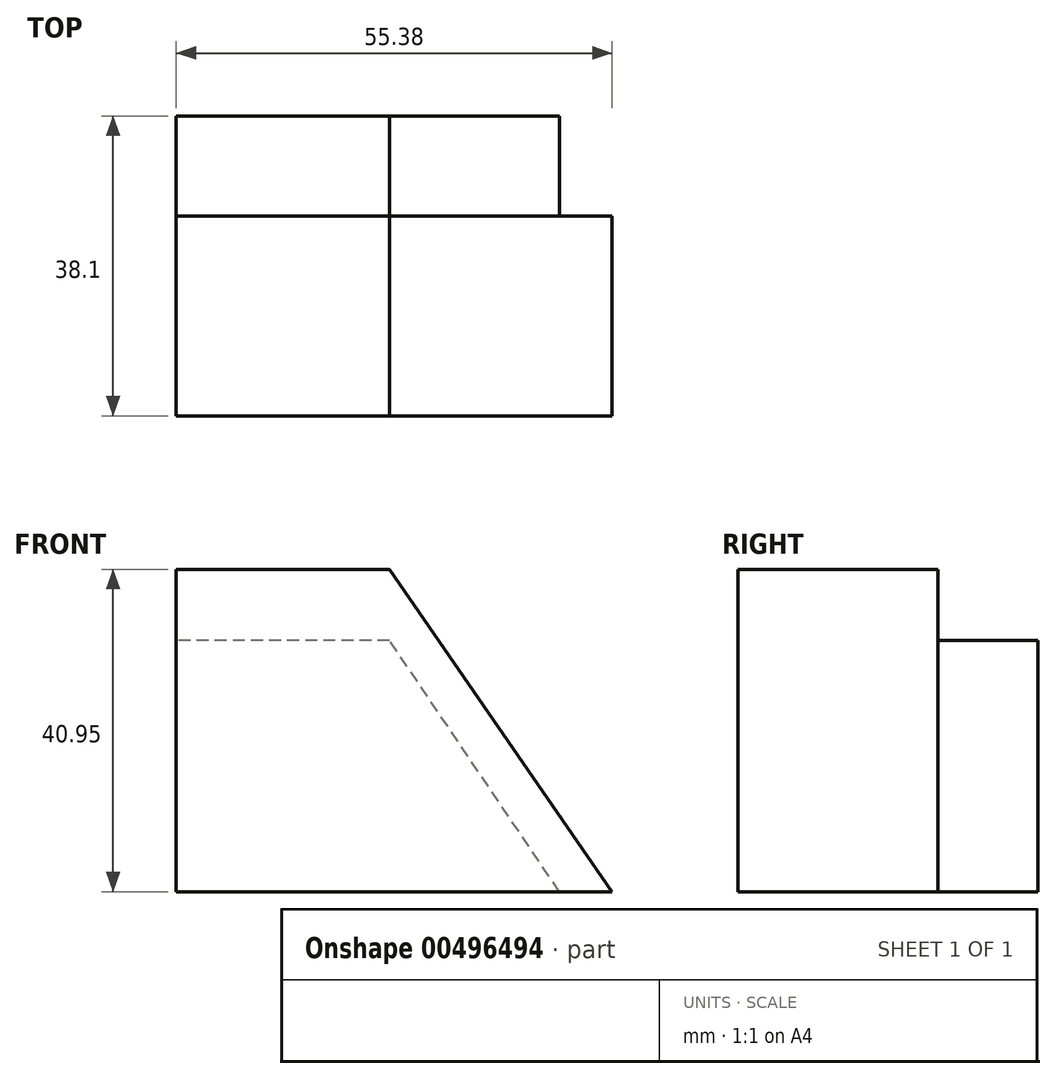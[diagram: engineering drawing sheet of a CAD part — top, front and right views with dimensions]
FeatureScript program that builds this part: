
annotation { "Feature Type Name" : "Feature", "Feature Type Description" : "" }
export const myFeature = defineFeature(function(context is Context, id is Id, definition is map)
    precondition{}
    {
        {
            var Q0;
            Q0=qCreatedBy(makeId("Front.planeOp"),FACE);
            var sketch = newSketch(context, id + "F0", { "sketchPlane" : qUnion([Q0])});
            skLineSegment(sketch, "E0", {"start": v(0, 0) * mm, "end": v(48.68, 0) * mm});
            skLineSegment(sketch, "E1", {"start": v(48.68, 0) * mm, "end": v(27.1, 31.92) * mm});
            skLineSegment(sketch, "E2", {"start": v(27.1, 31.92) * mm, "end": v(0, 31.92) * mm});
            skLineSegment(sketch, "E3", {"start": v(0, 31.92) * mm, "end": v(0, 0) * mm});
            skSolve(sketch);
        }
        {
            var Q0;
            Q0 = qSketchRegion(id + "F0", true);
            extrude(context, id + "F1", {"entities" : qUnion([Q0]), "oppositeDirection" : true, "depth" : 12.7 * mm});
        }
        {
            var Q0;
            Q0=qCreatedBy(makeId("Front.planeOp"),FACE);
            var sketch = newSketch(context, id + "F2", { "sketchPlane" : qUnion([Q0])});
            skLineSegment(sketch, "E4", {"start": v(0, 0) * mm, "end": v(0, 40.95) * mm});
            skLineSegment(sketch, "E5", {"start": v(0, 40.95) * mm, "end": v(27.1, 40.95) * mm});
            skLineSegment(sketch, "E6", {"start": v(27.1, 40.95) * mm, "end": v(55.38, 0) * mm});
            skLineSegment(sketch, "E7", {"start": v(55.38, 0) * mm, "end": v(0, 0) * mm});
            skSolve(sketch);
        }
        {
            var Q0;
            Q0=makeQuery(id+"F2.imprint","IMPRINT",FACE,{"disambiguationData":[TD([[makeQuery(id+"F2.imprint","IMPRINT",EDGE,{"derivedFrom":sQuery(id+"F2.wireOp",EDGE,"E4")}),-1.0]])]});
            extrude(context, id + "F3", {"entities" : qUnion([Q0]), "operationType" : NewBodyOperationType.ADD, "depth" : 25.4 * mm});
        }
    });
